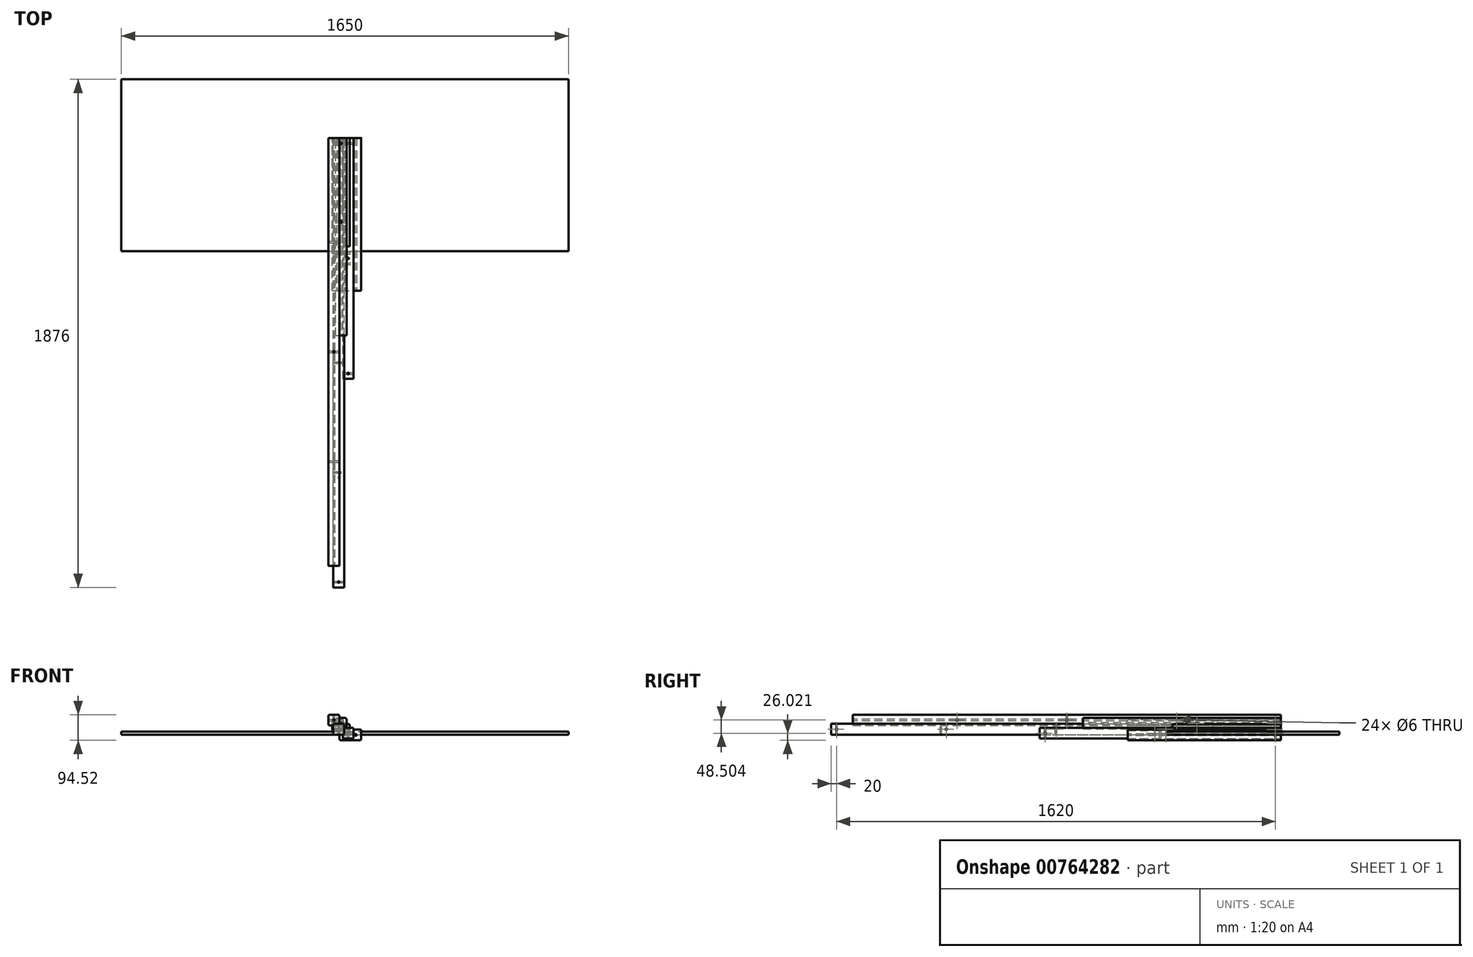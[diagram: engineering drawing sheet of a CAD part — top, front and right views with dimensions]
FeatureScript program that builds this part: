
annotation { "Feature Type Name" : "Feature", "Feature Type Description" : "" }
export const myFeature = defineFeature(function(context is Context, id is Id, definition is map)
    precondition{}
    {
        {
            var Q0;
            Q0=qCreatedBy(makeId("Front.planeOp"),FACE);
            var sketch = newSketch(context, id + "F0", { "sketchPlane" : qUnion([Q0])});
            skLineSegment(sketch, "E0.bottom", {"start": v(-13.8, 26.01) * mm, "end": v(26.2, 26.01) * mm});
            skLineSegment(sketch, "E0.top", {"start": v(-13.8, -13.99) * mm, "end": v(26.2, -13.99) * mm});
            skLineSegment(sketch, "E0.left", {"start": v(-13.8, 26.01) * mm, "end": v(-13.8, -13.99) * mm});
            skLineSegment(sketch, "E0.right", {"start": v(26.2, 26.01) * mm, "end": v(26.2, -13.99) * mm});
            skSolve(sketch);
        }
        {
            var Q0;
            Q0=makeQuery(id+"F0.imprint","IMPRINT",FACE,{"disambiguationData":[TD([[makeQuery(id+"F0.imprint","IMPRINT",EDGE,{"derivedFrom":sQuery(id+"F0.wireOp",EDGE,"E0.bottom")}),-1.0]])]});
            extrude(context, id + "F1", {"entities" : qUnion([Q0]), "depth" : 890 * mm, "offsetDistance" : 25 * mm});
        }
        {
            var Q0;
            Q0=makeQuery(id+"F1.opExtrude","SWEPT_EDGE",EDGE,{"disambiguationData":[OSD([sQuery(id+"F0.wireOp",EDGE,"E0.bottom"),sQuery(id+"F0.wireOp",EDGE,"E0.left")])]});
            var Q1;
            Q1=makeQuery(id+"F1.opExtrude","SWEPT_EDGE",EDGE,{"disambiguationData":[OSD([sQuery(id+"F0.wireOp",EDGE,"E0.bottom"),sQuery(id+"F0.wireOp",EDGE,"E0.right")])]});
            var Q2;
            Q2=makeQuery(id+"F1.opExtrude","SWEPT_EDGE",EDGE,{"disambiguationData":[OSD([sQuery(id+"F0.wireOp",EDGE,"E0.top"),sQuery(id+"F0.wireOp",EDGE,"E0.right")])]});
            var Q3;
            Q3=makeQuery(id+"F1.opExtrude","SWEPT_EDGE",EDGE,{"disambiguationData":[OSD([sQuery(id+"F0.wireOp",EDGE,"E0.top"),sQuery(id+"F0.wireOp",EDGE,"E0.left")])]});
            fillet(context, id + "F2", {"entities" : qUnion([Q0, Q1, Q2, Q3]), "radius" : 5 * mm, "tangentPropagation" : true, "allowEdgeOverflow" : false});
        }
        {
            var Q0;
            Q0=makeQuery(id+"F1.opExtrude","SWEPT_FACE",FACE,{"disambiguationData":[OSD([sQuery(id+"F0.wireOp",EDGE,"E0.bottom")])]});
            var sketch = newSketch(context, id + "F3", { "sketchPlane" : qUnion([Q0])});
            skPoint(sketch, "E1", {"position": v(6.2, -20) * mm});
            skPoint(sketch, "E2", {"position": v(6.2, -870) * mm});
            skPoint(sketch, "E3", {"position": v(6.2, -445) * mm});
            skSolve(sketch);
        }
        {
            var Q0;
            Q0=makeQuery(id+"F1.opExtrude","SWEPT_FACE",FACE,{"disambiguationData":[OSD([sQuery(id+"F0.wireOp",EDGE,"E0.right")])]});
            var sketch = newSketch(context, id + "F4", { "sketchPlane" : qUnion([Q0])});
            skPoint(sketch, "E4", {"position": v(-425, 6.01) * mm});
            skPoint(sketch, "E5", {"position": v(-465, 6.01) * mm});
            skPoint(sketch, "E6", {"position": v(-870, 6.01) * mm});
            skPoint(sketch, "E7", {"position": v(-40, 6.01) * mm});
            skPoint(sketch, "E7.positionSnap0", {"position": v(0, 6.01) * mm});
            skPoint(sketch, "E8", {"position": v(-850, 6.01) * mm});
            skPoint(sketch, "E9", {"position": v(-485, 6.01) * mm});
            skPoint(sketch, "E10", {"position": v(-405, 6.01) * mm});
            skPoint(sketch, "E11", {"position": v(-20, 6.01) * mm});
            skSolve(sketch);
        }
        {
            var Q0;
            Q0=sQuery(id+"F4.wireOp",VERTEX,"E6");
            var Q1;
            Q1=sQuery(id+"F4.wireOp",VERTEX,"E5");
            var Q2;
            Q2=sQuery(id+"F4.wireOp",VERTEX,"E4");
            var Q3;
            Q3=sQuery(id+"F3.wireOp",VERTEX,"E3");
            var Q4;
            Q4=sQuery(id+"F3.wireOp",VERTEX,"E1");
            var Q5;
            Q5=sQuery(id+"F3.wireOp",VERTEX,"E2");
            var Q6;
            Q6=sQuery(id+"F4.wireOp",VERTEX,"E11");
            var Q7;
            Q7=makeQuery(id+"F1.opExtrude","SWEPT_BODY",BODY,{"disambiguationData":[OSD([sQuery(id+"F0.wireOp",EDGE,"E0.bottom"),sQuery(id+"F0.wireOp",EDGE,"E0.top"),sQuery(id+"F0.wireOp",EDGE,"E0.left"),sQuery(id+"F0.wireOp",EDGE,"E0.right")])]});
            hole(context, id + "F5", {"style" : HoleStyle.SIMPLE, "endStyle" : HoleEndStyle.BLIND, "holeDiameter" : 6 * mm, "majorDiameter" : 5 * mm, "holeDepth" : 52 * mm, "isTappedThrough" : true, "tappedDepth" : 12 * mm, "tapClearance" : 3, "locations" : qUnion([Q0, Q1, Q2, Q3, Q4, Q5, Q6]), "scope" : qUnion([Q7])});
        }
        {
            var Q0;
            Q0=qCreatedBy(makeId("Front.planeOp"),FACE);
            var sketch = newSketch(context, id + "F6", { "sketchPlane" : qUnion([Q0])});
            skLineSegment(sketch, "E12.bottom", {"start": v(-28.58, 40) * mm, "end": v(11.42, 40) * mm});
            skLineSegment(sketch, "E12.top", {"start": v(-28.58, 0) * mm, "end": v(11.42, 0) * mm});
            skLineSegment(sketch, "E12.left", {"start": v(-28.58, 40) * mm, "end": v(-28.58, 0) * mm});
            skLineSegment(sketch, "E12.right", {"start": v(11.42, 40) * mm, "end": v(11.42, 0) * mm});
            skSolve(sketch);
        }
        {
            var Q0;
            Q0=makeQuery(id+"F6.imprint","IMPRINT",FACE,{"disambiguationData":[TD([[makeQuery(id+"F6.imprint","IMPRINT",EDGE,{"derivedFrom":sQuery(id+"F6.wireOp",EDGE,"E12.bottom")}),-1.0]])]});
            extrude(context, id + "F7", {"entities" : qUnion([Q0]), "depth" : 400 * mm, "offsetDistance" : 25 * mm});
        }
        {
            var Q0;
            Q0=makeQuery(id+"F7.opExtrude","SWEPT_EDGE",EDGE,{"disambiguationData":[OSD([sQuery(id+"F6.wireOp",EDGE,"E12.bottom"),sQuery(id+"F6.wireOp",EDGE,"E12.left")])]});
            var Q1;
            Q1=makeQuery(id+"F7.opExtrude","SWEPT_EDGE",EDGE,{"disambiguationData":[OSD([sQuery(id+"F6.wireOp",EDGE,"E12.bottom"),sQuery(id+"F6.wireOp",EDGE,"E12.right")])]});
            var Q2;
            Q2=makeQuery(id+"F7.opExtrude","SWEPT_EDGE",EDGE,{"disambiguationData":[OSD([sQuery(id+"F6.wireOp",EDGE,"E12.top"),sQuery(id+"F6.wireOp",EDGE,"E12.right")])]});
            var Q3;
            Q3=makeQuery(id+"F7.opExtrude","SWEPT_EDGE",EDGE,{"disambiguationData":[OSD([sQuery(id+"F6.wireOp",EDGE,"E12.top"),sQuery(id+"F6.wireOp",EDGE,"E12.left")])]});
            fillet(context, id + "F8", {"entities" : qUnion([Q0, Q1, Q2, Q3]), "radius" : 5 * mm, "tangentPropagation" : true, "allowEdgeOverflow" : false});
        }
        {
            var Q0;
            Q0=makeQuery(id+"F7.opExtrude","CAP_FACE",FACE,{"disambiguationData":[OSD([sQuery(id+"F6.wireOp",EDGE,"E12.bottom"),sQuery(id+"F6.wireOp",EDGE,"E12.top"),sQuery(id+"F6.wireOp",EDGE,"E12.left"),sQuery(id+"F6.wireOp",EDGE,"E12.right")])],"isStart":false});
            var sketch = newSketch(context, id + "F9", { "sketchPlane" : qUnion([Q0])});
            skPoint(sketch, "E13", {"position": v(-8.58, 20) * mm});
            skSolve(sketch);
        }
        {
            var Q0;
            Q0=sQuery(id+"F9.wireOp",VERTEX,"E13");
            var Q1;
            Q1=makeQuery(id+"F7.opExtrude","SWEPT_BODY",BODY,{"disambiguationData":[OSD([sQuery(id+"F6.wireOp",EDGE,"E12.bottom"),sQuery(id+"F6.wireOp",EDGE,"E12.top"),sQuery(id+"F6.wireOp",EDGE,"E12.left"),sQuery(id+"F6.wireOp",EDGE,"E12.right")])]});
            hole(context, id + "F10", {"style" : HoleStyle.SIMPLE, "endStyle" : HoleEndStyle.THROUGH, "holeDiameter" : 6 * mm, "majorDiameter" : 5 * mm, "isTappedThrough" : true, "tappedDepth" : 12 * mm, "tapClearance" : 3, "locations" : qUnion([Q0]), "scope" : qUnion([Q1])});
        }
        {
            var Q0;
            Q0=qCreatedBy(makeId("Front.planeOp"),FACE);
            var sketch = newSketch(context, id + "F11", { "sketchPlane" : qUnion([Q0])});
            skLineSegment(sketch, "E14.bottom", {"start": v(-25.71, 20) * mm, "end": v(54.29, 20) * mm});
            skLineSegment(sketch, "E14.top", {"start": v(-25.71, -20) * mm, "end": v(54.29, -20) * mm});
            skLineSegment(sketch, "E14.left", {"start": v(-25.71, 20) * mm, "end": v(-25.71, -20) * mm});
            skLineSegment(sketch, "E14.right", {"start": v(54.29, 20) * mm, "end": v(54.29, -20) * mm});
            skSolve(sketch);
        }
        {
            var Q0;
            Q0=makeQuery(id+"F11.imprint","IMPRINT",FACE,{"disambiguationData":[TD([[makeQuery(id+"F11.imprint","IMPRINT",EDGE,{"derivedFrom":sQuery(id+"F11.wireOp",EDGE,"E14.bottom")}),-1.0]])]});
            extrude(context, id + "F12", {"entities" : qUnion([Q0]), "depth" : 565 * mm, "offsetDistance" : 25 * mm});
        }
        {
            var Q0;
            Q0=makeQuery(id+"F12.opExtrude","SWEPT_EDGE",EDGE,{"disambiguationData":[OSD([sQuery(id+"F11.wireOp",EDGE,"E14.bottom"),sQuery(id+"F11.wireOp",EDGE,"E14.left")])]});
            var Q1;
            Q1=makeQuery(id+"F12.opExtrude","SWEPT_EDGE",EDGE,{"disambiguationData":[OSD([sQuery(id+"F11.wireOp",EDGE,"E14.bottom"),sQuery(id+"F11.wireOp",EDGE,"E14.right")])]});
            var Q2;
            Q2=makeQuery(id+"F12.opExtrude","SWEPT_EDGE",EDGE,{"disambiguationData":[OSD([sQuery(id+"F11.wireOp",EDGE,"E14.top"),sQuery(id+"F11.wireOp",EDGE,"E14.right")])]});
            var Q3;
            Q3=makeQuery(id+"F12.opExtrude","SWEPT_EDGE",EDGE,{"disambiguationData":[OSD([sQuery(id+"F11.wireOp",EDGE,"E14.top"),sQuery(id+"F11.wireOp",EDGE,"E14.left")])]});
            fillet(context, id + "F13", {"entities" : qUnion([Q0, Q1, Q2, Q3]), "radius" : 5 * mm, "tangentPropagation" : true, "allowEdgeOverflow" : false});
        }
        {
            var Q0;
            Q0=makeQuery(id+"F12.opExtrude","CAP_FACE",FACE,{"disambiguationData":[OSD([sQuery(id+"F11.wireOp",EDGE,"E14.bottom"),sQuery(id+"F11.wireOp",EDGE,"E14.top"),sQuery(id+"F11.wireOp",EDGE,"E14.left"),sQuery(id+"F11.wireOp",EDGE,"E14.right")])],"isStart":false});
            var sketch = newSketch(context, id + "F14", { "sketchPlane" : qUnion([Q0])});
            skPoint(sketch, "E15", {"position": v(-5.71, 0) * mm});
            skPoint(sketch, "E16", {"position": v(34.29, 0) * mm});
            skSolve(sketch);
        }
        {
            var Q0;
            Q0=sQuery(id+"F14.wireOp",VERTEX,"E15");
            var Q1;
            Q1=sQuery(id+"F14.wireOp",VERTEX,"E16");
            var Q2;
            Q2=makeQuery(id+"F12.opExtrude","SWEPT_BODY",BODY,{"disambiguationData":[OSD([sQuery(id+"F11.wireOp",EDGE,"E14.bottom"),sQuery(id+"F11.wireOp",EDGE,"E14.top"),sQuery(id+"F11.wireOp",EDGE,"E14.left"),sQuery(id+"F11.wireOp",EDGE,"E14.right")])]});
            hole(context, id + "F15", {"style" : HoleStyle.SIMPLE, "endStyle" : HoleEndStyle.THROUGH, "holeDiameter" : 6 * mm, "majorDiameter" : 5 * mm, "isTappedThrough" : true, "tappedDepth" : 12 * mm, "tapClearance" : 3, "locations" : qUnion([Q0, Q1]), "scope" : qUnion([Q2])});
        }
        {
            var Q0;
            Q0=qCreatedBy(makeId("Front.planeOp"),FACE);
            var sketch = newSketch(context, id + "F16", { "sketchPlane" : qUnion([Q0])});
            skLineSegment(sketch, "E17.bottom", {"start": v(-13.2, 15.9) * mm, "end": v(-53.2, 15.9) * mm});
            skLineSegment(sketch, "E17.top", {"start": v(-13.2, 55.9) * mm, "end": v(-53.2, 55.9) * mm});
            skLineSegment(sketch, "E17.left", {"start": v(-13.2, 15.9) * mm, "end": v(-13.2, 55.9) * mm});
            skLineSegment(sketch, "E17.right", {"start": v(-53.2, 15.9) * mm, "end": v(-53.2, 55.9) * mm});
            skSolve(sketch);
        }
        {
            var Q0;
            Q0=makeQuery(id+"F16.imprint","IMPRINT",FACE,{"disambiguationData":[TD([[makeQuery(id+"F16.imprint","IMPRINT",EDGE,{"derivedFrom":sQuery(id+"F16.wireOp",EDGE,"E17.bottom")}),-1.0]])]});
            extrude(context, id + "F17", {"entities" : qUnion([Q0]), "depth" : 565 * mm, "offsetDistance" : 25 * mm});
        }
        {
            var Q0;
            Q0=makeQuery(id+"F17.opExtrude","SWEPT_EDGE",EDGE,{"disambiguationData":[OSD([sQuery(id+"F16.wireOp",EDGE,"E17.top"),sQuery(id+"F16.wireOp",EDGE,"E17.right")])]});
            var Q1;
            Q1=makeQuery(id+"F17.opExtrude","SWEPT_EDGE",EDGE,{"disambiguationData":[OSD([sQuery(id+"F16.wireOp",EDGE,"E17.top"),sQuery(id+"F16.wireOp",EDGE,"E17.left")])]});
            var Q2;
            Q2=makeQuery(id+"F17.opExtrude","SWEPT_EDGE",EDGE,{"disambiguationData":[OSD([sQuery(id+"F16.wireOp",EDGE,"E17.bottom"),sQuery(id+"F16.wireOp",EDGE,"E17.left")])]});
            var Q3;
            Q3=makeQuery(id+"F17.opExtrude","SWEPT_EDGE",EDGE,{"disambiguationData":[OSD([sQuery(id+"F16.wireOp",EDGE,"E17.bottom"),sQuery(id+"F16.wireOp",EDGE,"E17.right")])]});
            fillet(context, id + "F18", {"entities" : qUnion([Q0, Q1, Q2, Q3]), "radius" : 5 * mm, "tangentPropagation" : true, "allowEdgeOverflow" : false});
        }
        {
            var Q0;
            Q0=makeQuery(id+"F17.opExtrude","CAP_FACE",FACE,{"disambiguationData":[OSD([sQuery(id+"F16.wireOp",EDGE,"E17.bottom"),sQuery(id+"F16.wireOp",EDGE,"E17.top"),sQuery(id+"F16.wireOp",EDGE,"E17.left"),sQuery(id+"F16.wireOp",EDGE,"E17.right")])],"isStart":false});
            var sketch = newSketch(context, id + "F19", { "sketchPlane" : qUnion([Q0])});
            skPoint(sketch, "E18", {"position": v(-33.2, 35.9) * mm});
            skSolve(sketch);
        }
        {
            var Q0;
            Q0=sQuery(id+"F19.wireOp",VERTEX,"E18");
            var Q1;
            Q1=makeQuery(id+"F17.opExtrude","SWEPT_BODY",BODY,{"disambiguationData":[OSD([sQuery(id+"F16.wireOp",EDGE,"E17.bottom"),sQuery(id+"F16.wireOp",EDGE,"E17.top"),sQuery(id+"F16.wireOp",EDGE,"E17.left"),sQuery(id+"F16.wireOp",EDGE,"E17.right")])]});
            hole(context, id + "F20", {"style" : HoleStyle.SIMPLE, "endStyle" : HoleEndStyle.THROUGH, "holeDiameter" : 6 * mm, "majorDiameter" : 5 * mm, "isTappedThrough" : true, "tappedDepth" : 12 * mm, "tapClearance" : 3, "locations" : qUnion([Q0]), "scope" : qUnion([Q1])});
        }
        {
            var Q0;
            Q0=qCreatedBy(makeId("Front.planeOp"),FACE);
            var sketch = newSketch(context, id + "F21", { "sketchPlane" : qUnion([Q0])});
            skLineSegment(sketch, "E19.bottom", {"start": v(-48.64, 40.8) * mm, "end": v(-8.64, 40.8) * mm});
            skLineSegment(sketch, "E19.top", {"start": v(-48.64, 0.8) * mm, "end": v(-8.64, 0.8) * mm});
            skLineSegment(sketch, "E19.left", {"start": v(-48.64, 40.8) * mm, "end": v(-48.64, 0.8) * mm});
            skLineSegment(sketch, "E19.right", {"start": v(-8.64, 40.8) * mm, "end": v(-8.64, 0.8) * mm});
            skSolve(sketch);
        }
        {
            var Q0;
            Q0=makeQuery(id+"F21.imprint","IMPRINT",FACE,{"disambiguationData":[TD([[makeQuery(id+"F21.imprint","IMPRINT",EDGE,{"derivedFrom":sQuery(id+"F21.wireOp",EDGE,"E19.bottom")}),-1.0]])]});
            extrude(context, id + "F22", {"entities" : qUnion([Q0]), "depth" : 1660 * mm, "offsetDistance" : 25 * mm});
        }
        {
            var Q0;
            Q0=makeQuery(id+"F22.opExtrude","SWEPT_EDGE",EDGE,{"disambiguationData":[OSD([sQuery(id+"F21.wireOp",EDGE,"E19.bottom"),sQuery(id+"F21.wireOp",EDGE,"E19.left")])]});
            var Q1;
            Q1=makeQuery(id+"F22.opExtrude","SWEPT_EDGE",EDGE,{"disambiguationData":[OSD([sQuery(id+"F21.wireOp",EDGE,"E19.bottom"),sQuery(id+"F21.wireOp",EDGE,"E19.right")])]});
            var Q2;
            Q2=makeQuery(id+"F22.opExtrude","SWEPT_EDGE",EDGE,{"disambiguationData":[OSD([sQuery(id+"F21.wireOp",EDGE,"E19.top"),sQuery(id+"F21.wireOp",EDGE,"E19.right")])]});
            var Q3;
            Q3=makeQuery(id+"F22.opExtrude","SWEPT_EDGE",EDGE,{"disambiguationData":[OSD([sQuery(id+"F21.wireOp",EDGE,"E19.top"),sQuery(id+"F21.wireOp",EDGE,"E19.left")])]});
            fillet(context, id + "F23", {"entities" : qUnion([Q0, Q1, Q2, Q3]), "radius" : 5 * mm, "tangentPropagation" : true, "allowEdgeOverflow" : false});
        }
        {
            var Q0;
            Q0=makeQuery(id+"F22.opExtrude","SWEPT_FACE",FACE,{"disambiguationData":[OSD([sQuery(id+"F21.wireOp",EDGE,"E19.right")])]});
            var sketch = newSketch(context, id + "F24", { "sketchPlane" : qUnion([Q0])});
            skPoint(sketch, "E20", {"position": v(-1640, 20.8) * mm});
            skPoint(sketch, "E21", {"position": v(-1636.39, 22.64) * mm});
            skPoint(sketch, "E22", {"position": v(-1620, 20.8) * mm});
            skPoint(sketch, "E23", {"position": v(-1255, 20.8) * mm});
            skPoint(sketch, "E24", {"position": v(-1235, 20.8) * mm});
            skPoint(sketch, "E25", {"position": v(-830, 20.8) * mm});
            skPoint(sketch, "E26", {"position": v(-425, 20.8) * mm});
            skPoint(sketch, "E27", {"position": v(-20, 20.01) * mm});
            skSolve(sketch);
        }
        {
            var Q0;
            Q0=makeQuery(id+"F22.opExtrude","SWEPT_FACE",FACE,{"disambiguationData":[OSD([sQuery(id+"F21.wireOp",EDGE,"E19.bottom")])]});
            var sketch = newSketch(context, id + "F25", { "sketchPlane" : qUnion([Q0])});
            skPoint(sketch, "E28", {"position": v(-28.64, -1640) * mm});
            skPoint(sketch, "E29", {"position": v(-28.64, -830) * mm});
            skPoint(sketch, "E30", {"position": v(-28.64, -20) * mm});
            skPoint(sketch, "E31", {"position": v(-28.64, -1255) * mm});
            skPoint(sketch, "E32", {"position": v(-28.64, -405) * mm});
            skSolve(sketch);
        }
        {
            var Q0;
            Q0=sQuery(id+"F25.wireOp",VERTEX,"E28");
            var Q1;
            Q1=sQuery(id+"F25.wireOp",VERTEX,"E31");
            var Q2;
            Q2=sQuery(id+"F25.wireOp",VERTEX,"E29");
            var Q3;
            Q3=sQuery(id+"F25.wireOp",VERTEX,"E32");
            var Q4;
            Q4=sQuery(id+"F25.wireOp",VERTEX,"E30");
            var Q5;
            Q5=sQuery(id+"F24.wireOp",VERTEX,"E27");
            var Q6;
            Q6=sQuery(id+"F24.wireOp",VERTEX,"E26");
            var Q7;
            Q7=sQuery(id+"F24.wireOp",VERTEX,"E25");
            var Q8;
            Q8=sQuery(id+"F24.wireOp",VERTEX,"E24");
            var Q9;
            Q9=sQuery(id+"F24.wireOp",VERTEX,"E20");
            var Q10;
            Q10=makeQuery(id+"F22.opExtrude","SWEPT_BODY",BODY,{"disambiguationData":[OSD([sQuery(id+"F21.wireOp",EDGE,"E19.bottom"),sQuery(id+"F21.wireOp",EDGE,"E19.top"),sQuery(id+"F21.wireOp",EDGE,"E19.left"),sQuery(id+"F21.wireOp",EDGE,"E19.right")])]});
            hole(context, id + "F26", {"style" : HoleStyle.SIMPLE, "endStyle" : HoleEndStyle.BLIND, "holeDiameter" : 6 * mm, "majorDiameter" : 5 * mm, "holeDepth" : 52 * mm, "isTappedThrough" : true, "tappedDepth" : 12 * mm, "tapClearance" : 3, "locations" : qUnion([Q0, Q1, Q2, Q3, Q4, Q5, Q6, Q7, Q8, Q9]), "scope" : qUnion([Q10])});
        }
        {
            var Q0;
            Q0=qCreatedBy(makeId("Front.planeOp"),FACE);
            var sketch = newSketch(context, id + "F27", { "sketchPlane" : qUnion([Q0])});
            skLineSegment(sketch, "E33.bottom", {"start": v(-51.86, 58.68) * mm, "end": v(-11.86, 58.68) * mm});
            skLineSegment(sketch, "E33.top", {"start": v(-51.86, 18.68) * mm, "end": v(-11.86, 18.68) * mm});
            skLineSegment(sketch, "E33.left", {"start": v(-51.86, 58.68) * mm, "end": v(-51.86, 18.68) * mm});
            skLineSegment(sketch, "E33.right", {"start": v(-11.86, 58.68) * mm, "end": v(-11.86, 18.68) * mm});
            skSolve(sketch);
        }
        {
            var Q0;
            Q0=makeQuery(id+"F27.imprint","IMPRINT",FACE,{"disambiguationData":[TD([[makeQuery(id+"F27.imprint","IMPRINT",EDGE,{"derivedFrom":sQuery(id+"F27.wireOp",EDGE,"E33.bottom")}),-1.0]])]});
            extrude(context, id + "F28", {"entities" : qUnion([Q0]), "depth" : 250 * mm, "offsetDistance" : 25 * mm});
        }
        {
            var Q0;
            Q0=makeQuery(id+"F28.opExtrude","SWEPT_EDGE",EDGE,{"disambiguationData":[OSD([sQuery(id+"F27.wireOp",EDGE,"E33.bottom"),sQuery(id+"F27.wireOp",EDGE,"E33.left")])]});
            var Q1;
            Q1=makeQuery(id+"F28.opExtrude","SWEPT_EDGE",EDGE,{"disambiguationData":[OSD([sQuery(id+"F27.wireOp",EDGE,"E33.bottom"),sQuery(id+"F27.wireOp",EDGE,"E33.right")])]});
            var Q2;
            Q2=makeQuery(id+"F28.opExtrude","SWEPT_EDGE",EDGE,{"disambiguationData":[OSD([sQuery(id+"F27.wireOp",EDGE,"E33.top"),sQuery(id+"F27.wireOp",EDGE,"E33.right")])]});
            var Q3;
            Q3=makeQuery(id+"F28.opExtrude","SWEPT_EDGE",EDGE,{"disambiguationData":[OSD([sQuery(id+"F27.wireOp",EDGE,"E33.top"),sQuery(id+"F27.wireOp",EDGE,"E33.left")])]});
            fillet(context, id + "F29", {"entities" : qUnion([Q0, Q1, Q2, Q3]), "radius" : 5 * mm, "tangentPropagation" : true, "allowEdgeOverflow" : false});
        }
        {
            var Q0;
            Q0=makeQuery(id+"F28.opExtrude","CAP_FACE",FACE,{"disambiguationData":[OSD([sQuery(id+"F27.wireOp",EDGE,"E33.bottom"),sQuery(id+"F27.wireOp",EDGE,"E33.top"),sQuery(id+"F27.wireOp",EDGE,"E33.left"),sQuery(id+"F27.wireOp",EDGE,"E33.right")])],"isStart":false});
            var sketch = newSketch(context, id + "F30", { "sketchPlane" : qUnion([Q0])});
            skPoint(sketch, "E34", {"position": v(-31.86, 38.68) * mm});
            skSolve(sketch);
        }
        {
            var Q0;
            Q0=sQuery(id+"F30.wireOp",VERTEX,"E34");
            var Q1;
            Q1=makeQuery(id+"F28.opExtrude","SWEPT_BODY",BODY,{"disambiguationData":[OSD([sQuery(id+"F27.wireOp",EDGE,"E33.bottom"),sQuery(id+"F27.wireOp",EDGE,"E33.top"),sQuery(id+"F27.wireOp",EDGE,"E33.left"),sQuery(id+"F27.wireOp",EDGE,"E33.right")])]});
            hole(context, id + "F31", {"style" : HoleStyle.SIMPLE, "endStyle" : HoleEndStyle.THROUGH, "holeDiameter" : 6 * mm, "majorDiameter" : 5 * mm, "isTappedThrough" : true, "tappedDepth" : 12 * mm, "tapClearance" : 3, "locations" : qUnion([Q0]), "scope" : qUnion([Q1])});
        }
        {
            var Q0;
            Q0=qCreatedBy(makeId("Front.planeOp"),FACE);
            var sketch = newSketch(context, id + "F32", { "sketchPlane" : qUnion([Q0])});
            skLineSegment(sketch, "E35.bottom", {"start": v(-40.07, 62.17) * mm, "end": v(-0.07, 62.17) * mm});
            skLineSegment(sketch, "E35.top", {"start": v(-40.07, 22.17) * mm, "end": v(-0.07, 22.17) * mm});
            skLineSegment(sketch, "E35.left", {"start": v(-40.07, 62.17) * mm, "end": v(-40.07, 22.17) * mm});
            skLineSegment(sketch, "E35.right", {"start": v(-0.07, 62.17) * mm, "end": v(-0.07, 22.17) * mm});
            skSolve(sketch);
        }
        {
            var Q0;
            Q0=makeQuery(id+"F32.imprint","IMPRINT",FACE,{"disambiguationData":[TD([[makeQuery(id+"F32.imprint","IMPRINT",EDGE,{"derivedFrom":sQuery(id+"F32.wireOp",EDGE,"E35.bottom")}),-1.0]])]});
            extrude(context, id + "F33", {"entities" : qUnion([Q0]), "depth" : 730 * mm, "offsetDistance" : 25 * mm});
        }
        {
            var Q0;
            Q0=makeQuery(id+"F33.opExtrude","SWEPT_EDGE",EDGE,{"disambiguationData":[OSD([sQuery(id+"F32.wireOp",EDGE,"E35.bottom"),sQuery(id+"F32.wireOp",EDGE,"E35.left")])]});
            var Q1;
            Q1=makeQuery(id+"F33.opExtrude","SWEPT_EDGE",EDGE,{"disambiguationData":[OSD([sQuery(id+"F32.wireOp",EDGE,"E35.bottom"),sQuery(id+"F32.wireOp",EDGE,"E35.right")])]});
            var Q2;
            Q2=makeQuery(id+"F33.opExtrude","SWEPT_EDGE",EDGE,{"disambiguationData":[OSD([sQuery(id+"F32.wireOp",EDGE,"E35.top"),sQuery(id+"F32.wireOp",EDGE,"E35.right")])]});
            var Q3;
            Q3=makeQuery(id+"F33.opExtrude","SWEPT_EDGE",EDGE,{"disambiguationData":[OSD([sQuery(id+"F32.wireOp",EDGE,"E35.top"),sQuery(id+"F32.wireOp",EDGE,"E35.left")])]});
            fillet(context, id + "F34", {"entities" : qUnion([Q0, Q1, Q2, Q3]), "radius" : 5 * mm, "tangentPropagation" : true, "allowEdgeOverflow" : false});
        }
        {
            var Q0;
            Q0=makeQuery(id+"F33.opExtrude","CAP_FACE",FACE,{"disambiguationData":[OSD([sQuery(id+"F32.wireOp",EDGE,"E35.bottom"),sQuery(id+"F32.wireOp",EDGE,"E35.top"),sQuery(id+"F32.wireOp",EDGE,"E35.left"),sQuery(id+"F32.wireOp",EDGE,"E35.right")])],"isStart":false});
            var sketch = newSketch(context, id + "F35", { "sketchPlane" : qUnion([Q0])});
            skPoint(sketch, "E36", {"position": v(-20.07, 42.17) * mm});
            skPoint(sketch, "E36.positionSnap0", {"position": v(-20.07, 22.17) * mm});
            skPoint(sketch, "E36.positionSnap1", {"position": v(-40.07, 42.17) * mm});
            skSolve(sketch);
        }
        {
            var Q0;
            Q0=makeQuery(id+"F33.opExtrude","SWEPT_FACE",FACE,{"disambiguationData":[OSD([sQuery(id+"F32.wireOp",EDGE,"E35.bottom")])]});
            var sketch = newSketch(context, id + "F36", { "sketchPlane" : qUnion([Q0])});
            skPoint(sketch, "E37", {"position": v(-20.07, -310) * mm});
            skPoint(sketch, "E38", {"position": v(-20.07, -20) * mm});
            skSolve(sketch);
        }
        {
            var Q0;
            Q0=makeQuery(id+"F33.opExtrude","SWEPT_FACE",FACE,{"disambiguationData":[OSD([sQuery(id+"F32.wireOp",EDGE,"E35.right")])]});
            var sketch = newSketch(context, id + "F37", { "sketchPlane" : qUnion([Q0])});
            skPoint(sketch, "E39", {"position": v(-310, 42.17) * mm});
            skPoint(sketch, "E40", {"position": v(-20, 42.17) * mm});
            skSolve(sketch);
        }
        {
            var Q0;
            Q0=sQuery(id+"F37.wireOp",VERTEX,"E40");
            var Q1;
            Q1=sQuery(id+"F37.wireOp",VERTEX,"E39");
            var Q2;
            Q2=sQuery(id+"F36.wireOp",VERTEX,"E38");
            var Q3;
            Q3=sQuery(id+"F36.wireOp",VERTEX,"E37");
            var Q4;
            Q4=sQuery(id+"F35.wireOp",VERTEX,"E36");
            var Q5;
            Q5=makeQuery(id+"F33.opExtrude","SWEPT_BODY",BODY,{"disambiguationData":[OSD([sQuery(id+"F32.wireOp",EDGE,"E35.bottom"),sQuery(id+"F32.wireOp",EDGE,"E35.top"),sQuery(id+"F32.wireOp",EDGE,"E35.left"),sQuery(id+"F32.wireOp",EDGE,"E35.right")])]});
            hole(context, id + "F38", {"style" : HoleStyle.SIMPLE, "endStyle" : HoleEndStyle.THROUGH, "holeDiameter" : 6 * mm, "majorDiameter" : 5 * mm, "isTappedThrough" : true, "tappedDepth" : 12 * mm, "tapClearance" : 3, "locations" : qUnion([Q0, Q1, Q2, Q3, Q4]), "scope" : qUnion([Q5])});
        }
        {
            var Q0;
            Q0=qCreatedBy(makeId("Front.planeOp"),FACE);
            var sketch = newSketch(context, id + "F39", { "sketchPlane" : qUnion([Q0])});
            skLineSegment(sketch, "E41.bottom", {"start": v(-66.54, 74.51) * mm, "end": v(-26.54, 74.51) * mm});
            skLineSegment(sketch, "E41.top", {"start": v(-66.54, 34.51) * mm, "end": v(-26.54, 34.51) * mm});
            skLineSegment(sketch, "E41.left", {"start": v(-66.54, 74.51) * mm, "end": v(-66.54, 34.51) * mm});
            skLineSegment(sketch, "E41.right", {"start": v(-26.54, 74.51) * mm, "end": v(-26.54, 34.51) * mm});
            skSolve(sketch);
        }
        {
            var Q0;
            Q0=makeQuery(id+"F39.imprint","IMPRINT",FACE,{"disambiguationData":[TD([[makeQuery(id+"F39.imprint","IMPRINT",EDGE,{"derivedFrom":sQuery(id+"F39.wireOp",EDGE,"E41.bottom")}),-1.0]])]});
            extrude(context, id + "F40", {"entities" : qUnion([Q0]), "depth" : 1580 * mm, "offsetDistance" : 25 * mm});
        }
        {
            var Q0;
            Q0=makeQuery(id+"F40.opExtrude","SWEPT_EDGE",EDGE,{"disambiguationData":[OSD([sQuery(id+"F39.wireOp",EDGE,"E41.bottom"),sQuery(id+"F39.wireOp",EDGE,"E41.left")])]});
            var Q1;
            Q1=makeQuery(id+"F40.opExtrude","SWEPT_EDGE",EDGE,{"disambiguationData":[OSD([sQuery(id+"F39.wireOp",EDGE,"E41.bottom"),sQuery(id+"F39.wireOp",EDGE,"E41.right")])]});
            var Q2;
            Q2=makeQuery(id+"F40.opExtrude","SWEPT_EDGE",EDGE,{"disambiguationData":[OSD([sQuery(id+"F39.wireOp",EDGE,"E41.top"),sQuery(id+"F39.wireOp",EDGE,"E41.right")])]});
            var Q3;
            Q3=makeQuery(id+"F40.opExtrude","SWEPT_EDGE",EDGE,{"disambiguationData":[OSD([sQuery(id+"F39.wireOp",EDGE,"E41.top"),sQuery(id+"F39.wireOp",EDGE,"E41.left")])]});
            fillet(context, id + "F41", {"entities" : qUnion([Q0, Q1, Q2, Q3]), "radius" : 5 * mm, "tangentPropagation" : true, "allowEdgeOverflow" : false});
        }
        {
            var Q0;
            Q0=makeQuery(id+"F40.opExtrude","CAP_FACE",FACE,{"disambiguationData":[OSD([sQuery(id+"F39.wireOp",EDGE,"E41.bottom"),sQuery(id+"F39.wireOp",EDGE,"E41.top"),sQuery(id+"F39.wireOp",EDGE,"E41.left"),sQuery(id+"F39.wireOp",EDGE,"E41.right")])],"isStart":false});
            var sketch = newSketch(context, id + "F42", { "sketchPlane" : qUnion([Q0])});
            skPoint(sketch, "E42", {"position": v(-46.54, 54.51) * mm});
            skPoint(sketch, "E42.positionSnap0", {"position": v(-46.54, 34.51) * mm});
            skPoint(sketch, "E42.positionSnap1", {"position": v(-66.54, 54.51) * mm});
            skSolve(sketch);
        }
        {
            var Q0;
            Q0=makeQuery(id+"F40.opExtrude","SWEPT_FACE",FACE,{"disambiguationData":[OSD([sQuery(id+"F39.wireOp",EDGE,"E41.right")])]});
            var sketch = newSketch(context, id + "F43", { "sketchPlane" : qUnion([Q0])});
            skPoint(sketch, "E43", {"position": v(-1195, 54.51) * mm});
            skPoint(sketch, "E44", {"position": v(-790, 54.51) * mm});
            skPoint(sketch, "E45", {"position": v(-385, 54.51) * mm});
            skSolve(sketch);
        }
        {
            var Q0;
            Q0=sQuery(id+"F43.wireOp",VERTEX,"E43");
            var Q1;
            Q1=sQuery(id+"F42.wireOp",VERTEX,"E42");
            var Q2;
            Q2=sQuery(id+"F43.wireOp",VERTEX,"E44");
            var Q3;
            Q3=sQuery(id+"F43.wireOp",VERTEX,"E45");
            var Q4;
            Q4=makeQuery(id+"F40.opExtrude","SWEPT_BODY",BODY,{"disambiguationData":[OSD([sQuery(id+"F39.wireOp",EDGE,"E41.bottom"),sQuery(id+"F39.wireOp",EDGE,"E41.top"),sQuery(id+"F39.wireOp",EDGE,"E41.left"),sQuery(id+"F39.wireOp",EDGE,"E41.right")])]});
            hole(context, id + "F44", {"style" : HoleStyle.SIMPLE, "endStyle" : HoleEndStyle.THROUGH, "holeDiameter" : 6 * mm, "majorDiameter" : 5 * mm, "isTappedThrough" : true, "tappedDepth" : 12 * mm, "tapClearance" : 3, "locations" : qUnion([Q0, Q1, Q2, Q3]), "scope" : qUnion([Q4])});
        }
        {
            var Q0;
            Q0=makeQuery(id+"F40.opExtrude","SWEPT_FACE",FACE,{"disambiguationData":[OSD([sQuery(id+"F39.wireOp",EDGE,"E41.bottom")])]});
            var sketch = newSketch(context, id + "F45", { "sketchPlane" : qUnion([Q0])});
            skPoint(sketch, "E46", {"position": v(-46.5, -790) * mm});
            skSolve(sketch);
        }
        {
            var Q0;
            Q0=sQuery(id+"F45.wireOp",VERTEX,"E46");
            var Q1;
            Q1=makeQuery(id+"F40.opExtrude","SWEPT_BODY",BODY,{"disambiguationData":[OSD([sQuery(id+"F39.wireOp",EDGE,"E41.bottom"),sQuery(id+"F39.wireOp",EDGE,"E41.top"),sQuery(id+"F39.wireOp",EDGE,"E41.left"),sQuery(id+"F39.wireOp",EDGE,"E41.right")])]});
            hole(context, id + "F46", {"style" : HoleStyle.SIMPLE, "endStyle" : HoleEndStyle.THROUGH, "holeDiameter" : 6 * mm, "majorDiameter" : 5 * mm, "isTappedThrough" : true, "tappedDepth" : 12 * mm, "tapClearance" : 3, "locations" : qUnion([Q0]), "scope" : qUnion([Q1])});
        }
        {
            var Q0;
            Q0=qCreatedBy(makeId("Top.planeOp"),FACE);
            var sketch = newSketch(context, id + "F47", { "sketchPlane" : qUnion([Q0])});
            skLineSegment(sketch, "E47.bottom", {"start": v(-830.74, 216) * mm, "end": v(819.26, 216) * mm});
            skLineSegment(sketch, "E47.top", {"start": v(-830.74, -419) * mm, "end": v(819.26, -419) * mm});
            skLineSegment(sketch, "E47.left", {"start": v(-830.74, 216) * mm, "end": v(-830.74, -419) * mm});
            skLineSegment(sketch, "E47.right", {"start": v(819.26, 216) * mm, "end": v(819.26, -419) * mm});
            skSolve(sketch);
        }
        {
            var Q0;
            Q0=makeQuery(id+"F47.imprint","IMPRINT",FACE,{"disambiguationData":[TD([[makeQuery(id+"F47.imprint","IMPRINT",EDGE,{"derivedFrom":sQuery(id+"F47.wireOp",EDGE,"E47.bottom")}),-1.0]])]});
            extrude(context, id + "F48", {"entities" : qUnion([Q0]), "depth" : 12 * mm, "offsetDistance" : 25 * mm});
        }
    });
